# Revit family: TR3102
name_source: partatom
category: Verbindungsmittel
units: mm (PartAtom-declared; Revit-internal decimal feet)

## family parameters
Arbeitsebenenbasiert = Nein
Beim Laden mit Abzugskörper schneiden = Nein
Gemeinsam genutzt = Nein
Immer vertikal = Nein
OmniClass-Nummer = 23.25.10.27.11.21
OmniClass-Titel = Reinforcement Couplers

## types (9) — shared parameters
Endenbearbeitung 1 = Mit Gewinde
Endenbearbeitung 2 = Mit Gewinde
Hersteller = Stahlwerk Annahütte Max Aicher GmbH Co.KG
Modell = TR 3102
TR3102-G_Vis = Ja
TR3102-L_Vis = Ja
Typenbild = TR3102.png
URL = http//:www.annahuette.com

## per-type parameters (varying)
| type | Außendurchmesser | Beschreibung | Einfassung Stab 1 | Einfassung Stab 2 | Gesamtlänge | Körper | Stabgröße 1 | Stabgröße 2 | TR3102-G | TR3102-L | TR3102-L0 | TR3102-L1 | TR3102-L2 | TR3102-Stab1 | TR3102-Stab2 | TR3102-ød | Typenkommentare |
| TR 3102-ø22/18 | 40 mm  [stored 0.131234 ft] | TR3102-ø22/18 | 55 mm  [stored 0.180446 ft] | 50 mm  [stored 0.164042 ft] | 145 mm  [stored 0.475722 ft] | 1,00 kg | SAS 670 - ø22 | SAS 670 - ø18 | 1,00 kg | 145 mm  [stored 0.475722 ft] | 73 mm | 55 mm  [stored 0.180446 ft] | 50 mm  [stored 0.164042 ft] | 22 mm  [stored 0.0721785 ft] | 18 mm  [stored 0.0590551 ft] | 40 mm  [stored 0.131234 ft] | TR 3102 - Reduziermuffe |
| TR 3102-ø25/22 | 45 mm  [stored 0.147638 ft] | TR3102-ø25/22 | 60 mm  [stored 0.19685 ft] | 55 mm  [stored 0.180446 ft] | 160 mm  [stored 0.524934 ft] | 1,40 kg | SAS 670 - ø25 | SAS 670 - ø22 | 1,40 kg | 160 mm  [stored 0.524934 ft] | 80 mm  [stored 0.262467 ft] | 60 mm  [stored 0.19685 ft] | 55 mm  [stored 0.180446 ft] | 25 mm  [stored 0.082021 ft] | 22 mm  [stored 0.0721785 ft] | 45 mm  [stored 0.147638 ft] | TR 3102 - Reduziermuffe |
| TR 3102-ø28/25 | 50 mm  [stored 0.164042 ft] | TR3102-ø28/25 | 70 mm  [stored 0.229659 ft] | 60 mm  [stored 0.19685 ft] | 180 mm  [stored 0.590551 ft] | 2,00 kg | SAS 670 - ø28 | SAS 670 - ø25 | 2,00 kg | 180 mm  [stored 0.590551 ft] | 90 mm  [stored 0.295276 ft] | 70 mm  [stored 0.229659 ft] | 60 mm  [stored 0.19685 ft] | 28 mm  [stored 0.0918635 ft] | 25 mm  [stored 0.082021 ft] | 50 mm  [stored 0.164042 ft] | TR 3102 - Reduziermuffe |
| TR 3102-ø30/28 | 55 mm  [stored 0.180446 ft] | TR3102-ø30/28 | 75 mm | 70 mm  [stored 0.229659 ft] | 195 mm  [stored 0.639764 ft] | 2,50 kg | SAS 670 - ø30 | SAS 670 - ø28 | 2,50 kg | 195 mm  [stored 0.639764 ft] | 98 mm | 75 mm | 70 mm  [stored 0.229659 ft] | 30 mm  [stored 0.0984252 ft] | 28 mm  [stored 0.0918635 ft] | 55 mm  [stored 0.180446 ft] | TR 3102 - Reduziermuffe |
| TR 3102-ø35/30 | 60 mm  [stored 0.19685 ft] | TR3102-ø35/30 | 85 mm  [stored 0.278871 ft] | 75 mm | 215 mm | 3,00 kg | SAS 670 - ø35 | SAS 670 - ø30 | 3,00 kg | 215 mm | 108 mm | 85 mm  [stored 0.278871 ft] | 75 mm | 35 mm  [stored 0.114829 ft] | 30 mm  [stored 0.0984252 ft] | 60 mm  [stored 0.19685 ft] | TR 3102 - Rduziermuffe |
| TR 3102-ø43/35 | 80 mm  [stored 0.262467 ft] | TR3102-ø43/35 | 100 mm  [stored 0.328084 ft] | 85 mm  [stored 0.278871 ft] | 250 mm  [stored 0.82021 ft] | 5,50 kg | SAS 670 - ø43 | SAS 670 - ø35 | 5,50 kg | 250 mm  [stored 0.82021 ft] | 125 mm  [stored 0.410105 ft] | 100 mm  [stored 0.328084 ft] | 85 mm  [stored 0.278871 ft] | 43 mm  [stored 0.141076 ft] | 35 mm  [stored 0.114829 ft] | 80 mm  [stored 0.262467 ft] | TR 3102 - Reduziermuffe |
| TR 3102-ø57,5/50 | 100 mm  [stored 0.328084 ft] | TR3102-ø57,5/50 | 125 mm  [stored 0.410105 ft] | 105 mm  [stored 0.344488 ft] | 295 mm  [stored 0.967848 ft] | 11,94 kg | SAS 670 - ø57,5 | SAS 670 - ø50 | 11,94 kg | 295 mm  [stored 0.967848 ft] | 148 mm | 125 mm  [stored 0.410105 ft] | 105 mm  [stored 0.344488 ft] | 58 mm | 50 mm  [stored 0.164042 ft] | 100 mm  [stored 0.328084 ft] | TR 3102 - Reduziermuffe |
| TR 3102-ø63,5/57,5 | 110 mm  [stored 0.360892 ft] | TR3102-ø63,5/57,5 | 130 mm  [stored 0.426509 ft] | 125 mm  [stored 0.410105 ft] | 305 mm  [stored 1.00066 ft] | 14,89 kg | SAS 670 - ø63,5 | SAS 670 - ø57,5 | 14,89 kg | 305 mm  [stored 1.00066 ft] | 153 mm | 130 mm  [stored 0.426509 ft] | 125 mm  [stored 0.410105 ft] | 64 mm | 58 mm | 110 mm  [stored 0.360892 ft] | TR 3102 - Reduziermuffe |
| TR 3102-ø50/43 | 85 mm  [stored 0.278871 ft] | TR3102-ø50/43 | 105 mm  [stored 0.344488 ft] | 100 mm  [stored 0.328084 ft] | 270 mm  [stored 0.885827 ft] | 7,68 kg | SAS 670 - ø50 | SAS 670 - ø43 | 7,68 kg | 270 mm  [stored 0.885827 ft] | 135 mm  [stored 0.442913 ft] | 105 mm  [stored 0.344488 ft] | 100 mm  [stored 0.328084 ft] | 50 mm  [stored 0.164042 ft] | 43 mm  [stored 0.141076 ft] | 85 mm  [stored 0.278871 ft] | TR 3102 - Reduziermuffe |

note: [stored X ft] marks values corroborated as IEEE doubles in the binary element streams (Revit-internal decimal feet)
